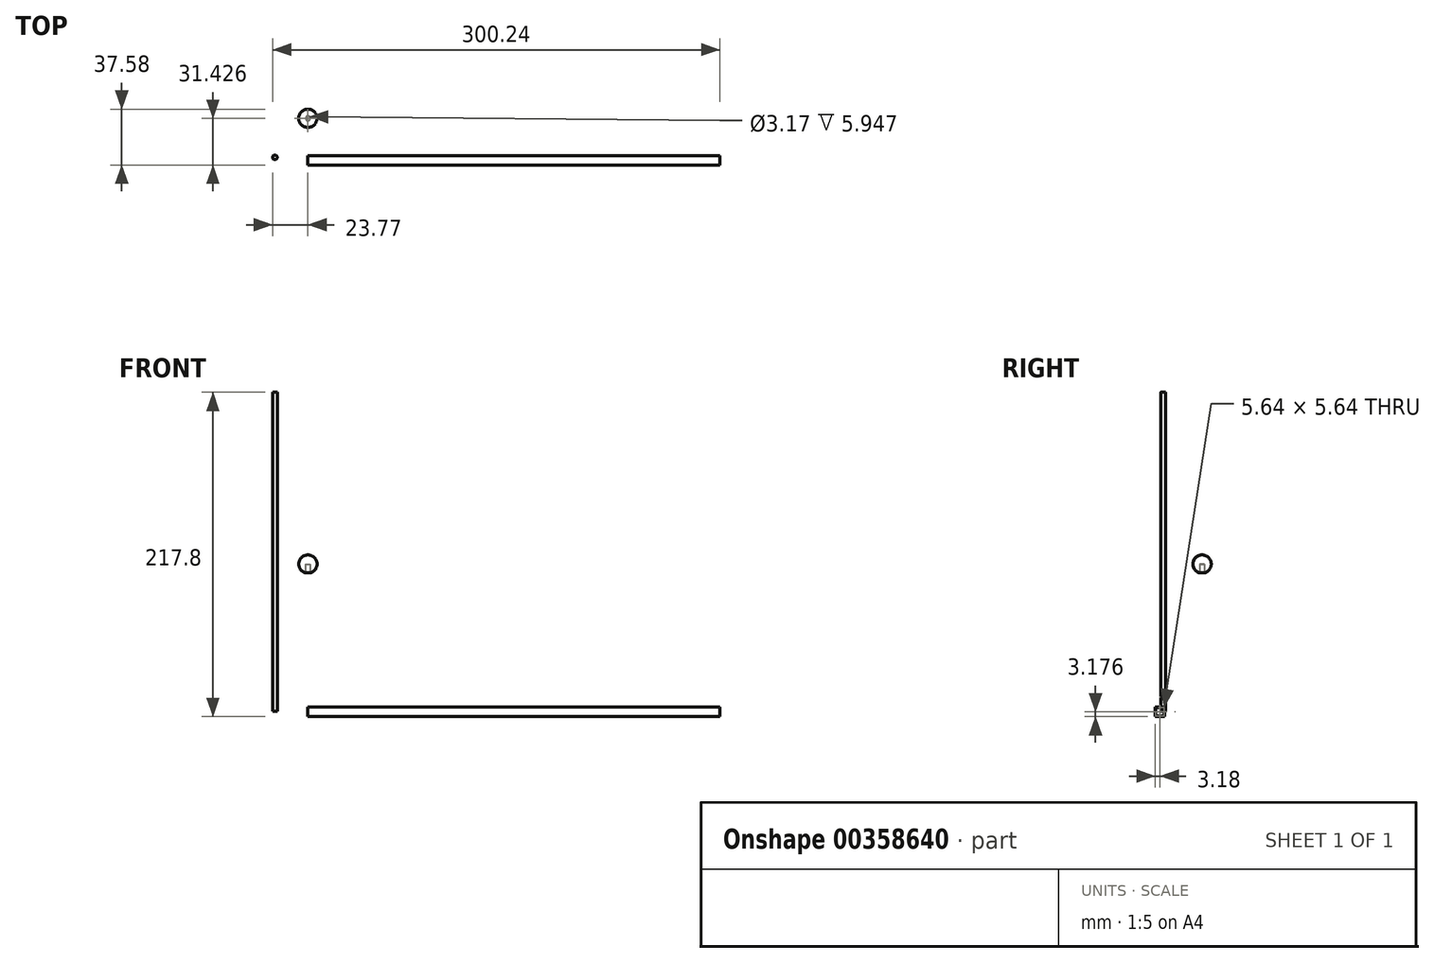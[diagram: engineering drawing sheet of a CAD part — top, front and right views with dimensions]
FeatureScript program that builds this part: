
annotation { "Feature Type Name" : "Feature", "Feature Type Description" : "" }
export const myFeature = defineFeature(function(context is Context, id is Id, definition is map)
    precondition{}
    {
        {
            assignVariable(context, id + "F0", {"name" : "Rod", "anyValue" : 237.1 - 22.78});
        }
        {
            assignVariable(context, id + "F1", {"name" : "Tube", "anyValue" : 276.47});
        }
        {
            var Q0;
            Q0=qCreatedBy(makeId("Right.planeOp"),FACE);
            var sketch = newSketch(context, id + "F2", { "sketchPlane" : qUnion([Q0])});
            skArc(sketch, "E0", {"start": v(28.59, 105.1) * mm, "mid": v(22.48, 99.74) * mm, "end": v(27, 92.99) * mm});
            skLineSegment(sketch, "E1", {"start": v(28.59, 98.94) * mm, "end": v(28.59, 105.1) * mm});
            skLineSegment(sketch, "E2", {"start": v(28.59, 98.94) * mm, "end": v(27, 98.94) * mm});
            skLineSegment(sketch, "E3", {"start": v(27, 98.94) * mm, "end": v(27, 92.99) * mm});
            skSolve(sketch);
        }
        {
            var Q0;
            Q0=makeQuery(id+"F2.imprint","IMPRINT",FACE,{"disambiguationData":[TD([[makeQuery(id+"F2.imprint","IMPRINT",EDGE,{"derivedFrom":sQuery(id+"F2.wireOp",EDGE,"E0")}),1.0]])]});
            var Q1;
            Q1=sQuery(id+"F2.wireOp",EDGE,"E1");
            revolve(context, id + "F3", {"entities" : qUnion([Q0]), "axis" : qUnion([Q1]), "revolveType" : RevolveType.FULL});
        }
        {
            var Q0;
            Q0=qCreatedBy(makeId("Right.planeOp"),FACE);
            var sketch = newSketch(context, id + "F4", { "sketchPlane" : qUnion([Q0])});
            skLineSegment(sketch, "E4.bottom", {"start": v(-2.84, 2.87) * mm, "end": v(3.51, 2.87) * mm});
            skLineSegment(sketch, "E4.top", {"start": v(-2.84, -3.48) * mm, "end": v(3.51, -3.48) * mm});
            skLineSegment(sketch, "E4.left", {"start": v(-2.84, 2.87) * mm, "end": v(-2.84, -3.48) * mm});
            skLineSegment(sketch, "E4.right", {"start": v(3.51, 2.87) * mm, "end": v(3.51, -3.48) * mm});
            skLineSegment(sketch, "E5.bottom", {"start": v(-2.48, 2.52) * mm, "end": v(3.16, 2.52) * mm});
            skLineSegment(sketch, "E5.top", {"start": v(-2.48, -3.12) * mm, "end": v(3.16, -3.12) * mm});
            skLineSegment(sketch, "E5.left", {"start": v(-2.48, 2.52) * mm, "end": v(-2.48, -3.12) * mm});
            skLineSegment(sketch, "E5.right", {"start": v(3.16, 2.52) * mm, "end": v(3.16, -3.12) * mm});
            skSolve(sketch);
        }
        {
            var Q0;
            Q0=makeQuery(id+"F4.imprint","IMPRINT",FACE,{"disambiguationData":[TD([[makeQuery(id+"F4.imprint","IMPRINT",EDGE,{"derivedFrom":sQuery(id+"F4.wireOp",EDGE,"E4.bottom")}),-1.0]])]});
            extrude(context, id + "F5", {"entities" : qUnion([Q0]), "depth" : (getVariable(context, 'Tube')) * mm, "offsetDistance" : 25 * mm});
        }
        {
            var Q0;
            Q0=qCreatedBy(makeId("Top.planeOp"),FACE);
            var sketch = newSketch(context, id + "F6", { "sketchPlane" : qUnion([Q0])});
            skCircle(sketch, "E6", {"center": v(-22.19, 2.38) * mm, "radius": 1.59 * mm});
            skSolve(sketch);
        }
        {
            var Q0;
            Q0=makeQuery(id+"F6.imprint","IMPRINT",FACE,{"disambiguationData":[TD([[makeQuery(id+"F6.imprint","IMPRINT",EDGE,{"derivedFrom":sQuery(id+"F6.wireOp",EDGE,"E6")}),1.0]])]});
            extrude(context, id + "F7", {"entities" : qUnion([Q0]), "depth" : (getVariable(context, 'Rod')) * mm, "offsetDistance" : 25 * mm});
        }
    });
